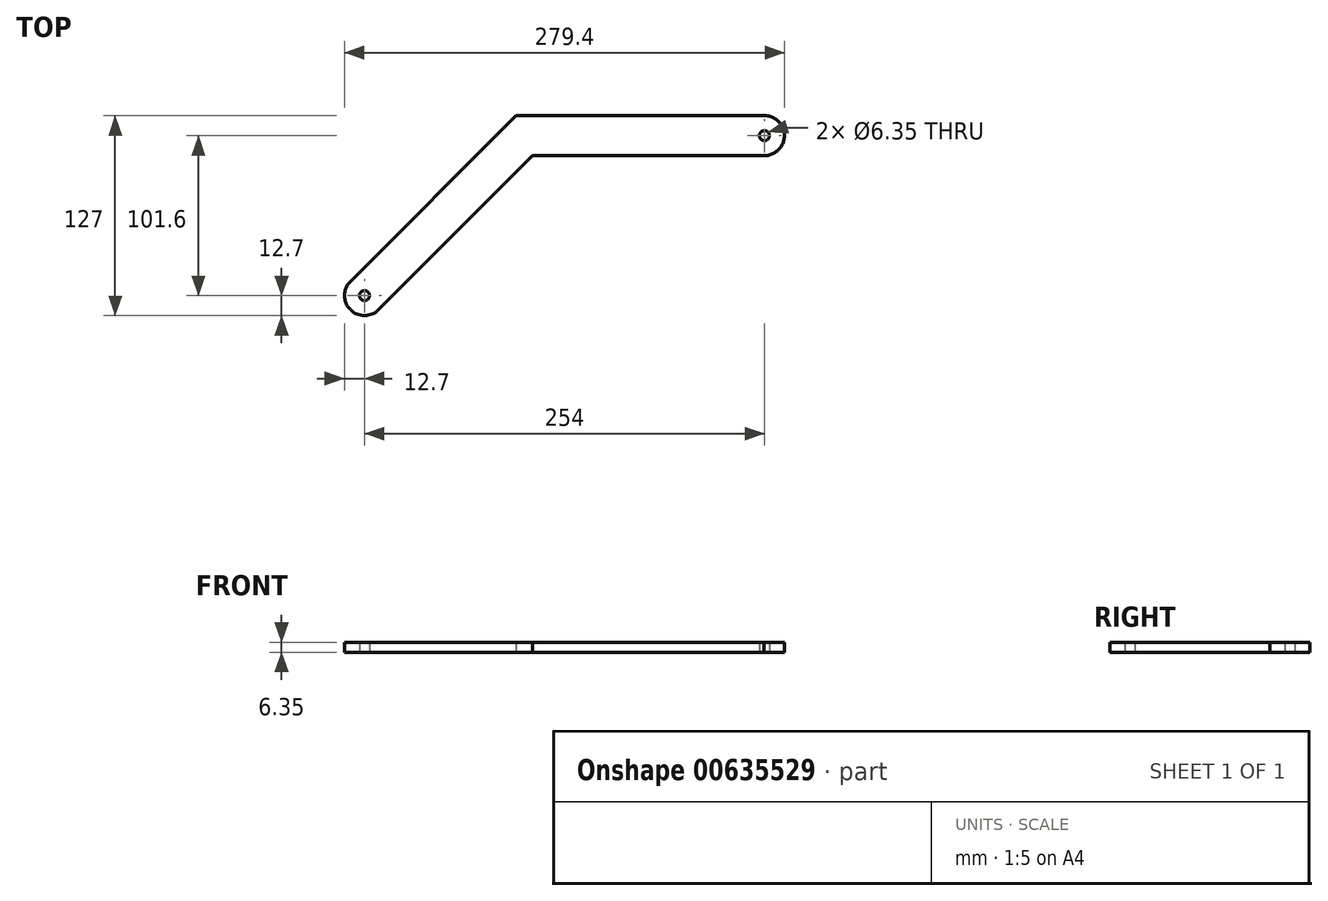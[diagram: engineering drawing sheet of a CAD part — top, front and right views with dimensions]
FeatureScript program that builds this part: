
annotation { "Feature Type Name" : "Feature", "Feature Type Description" : "" }
export const myFeature = defineFeature(function(context is Context, id is Id, definition is map)
    precondition{}
    {
        {
            var Q0;
            Q0=qCreatedBy(makeId("Top.planeOp"),FACE);
            var sketch = newSketch(context, id + "F0", { "sketchPlane" : qUnion([Q0])});
            skCircle(sketch, "E0", {"center": v(0, 0) * mm, "radius": 3.18 * mm});
            skCircle(sketch, "E1", {"center": v(254, 101.6) * mm, "radius": 3.18 * mm});
            skLineSegment(sketch, "E2", {"start": v(254, 101.6) * mm, "end": v(101.6, 101.6) * mm});
            skLineSegment(sketch, "E3", {"start": v(0, 0) * mm, "end": v(101.6, 101.6) * mm});
            skArc(sketch, "E4", {"start": v(-8.98, 8.98) * mm, "mid": v(-8.98, -8.98) * mm, "end": v(8.98, -8.98) * mm});
            skArc(sketch, "E5", {"start": v(253.57, 88.9) * mm, "mid": v(266.7, 101.53) * mm, "end": v(253.71, 114.3) * mm});
            skLineSegment(sketch, "E6", {"start": v(254.43, 88.9) * mm, "end": v(106.87, 88.9) * mm});
            skLineSegment(sketch, "E7", {"start": v(254.29, 114.3) * mm, "end": v(96.34, 114.3) * mm});
            skLineSegment(sketch, "E8", {"start": v(-8.98, 8.98) * mm, "end": v(96.34, 114.3) * mm});
            skLineSegment(sketch, "E9", {"start": v(8.98, -8.98) * mm, "end": v(106.87, 88.9) * mm});
            skSolve(sketch);
        }
        {
            var Q0;
            Q0 = qSketchRegion(id + "F0", true);
            extrude(context, id + "F1", {"entities" : qUnion([Q0]), "depth" : 6.35 * mm, "offsetDistance" : 25.4 * mm});
        }
    });
